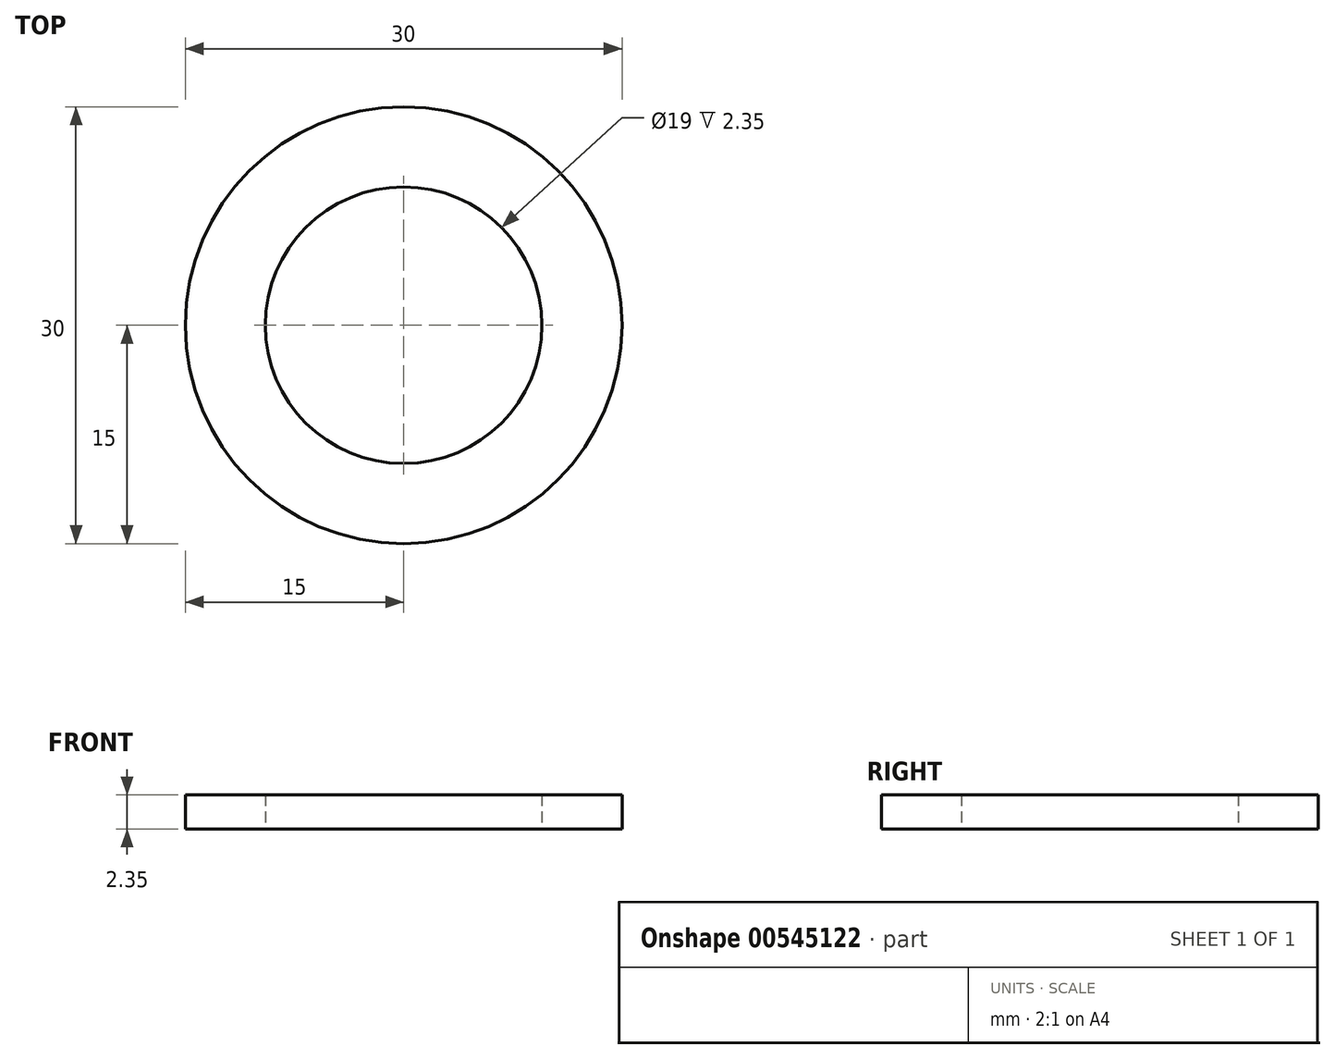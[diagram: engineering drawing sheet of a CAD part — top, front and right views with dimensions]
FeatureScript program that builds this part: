
annotation { "Feature Type Name" : "Feature", "Feature Type Description" : "" }
export const myFeature = defineFeature(function(context is Context, id is Id, definition is map)
    precondition{}
    {
        {
            var Q0;
            Q0=qCreatedBy(makeId("Top.planeOp"),FACE);
            var sketch = newSketch(context, id + "F0", { "sketchPlane" : qUnion([Q0])});
            skCircle(sketch, "E0", {"center": v(0, 0) * mm, "radius": 15 * mm});
            skCircle(sketch, "E1", {"center": v(0, 0) * mm, "radius": 9.5 * mm});
            skSolve(sketch);
        }
        {
            var Q0;
            Q0=makeQuery(id+"F0.imprint","IMPRINT",FACE,{"disambiguationData":[TD([[makeQuery(id+"F0.imprint","IMPRINT",EDGE,{"derivedFrom":sQuery(id+"F0.wireOp",EDGE,"E0")}),1.0]])]});
            extrude(context, id + "F1", {"entities" : qUnion([Q0]), "depth" : 2.35 * mm, "offsetDistance" : 25 * mm});
        }
    });
